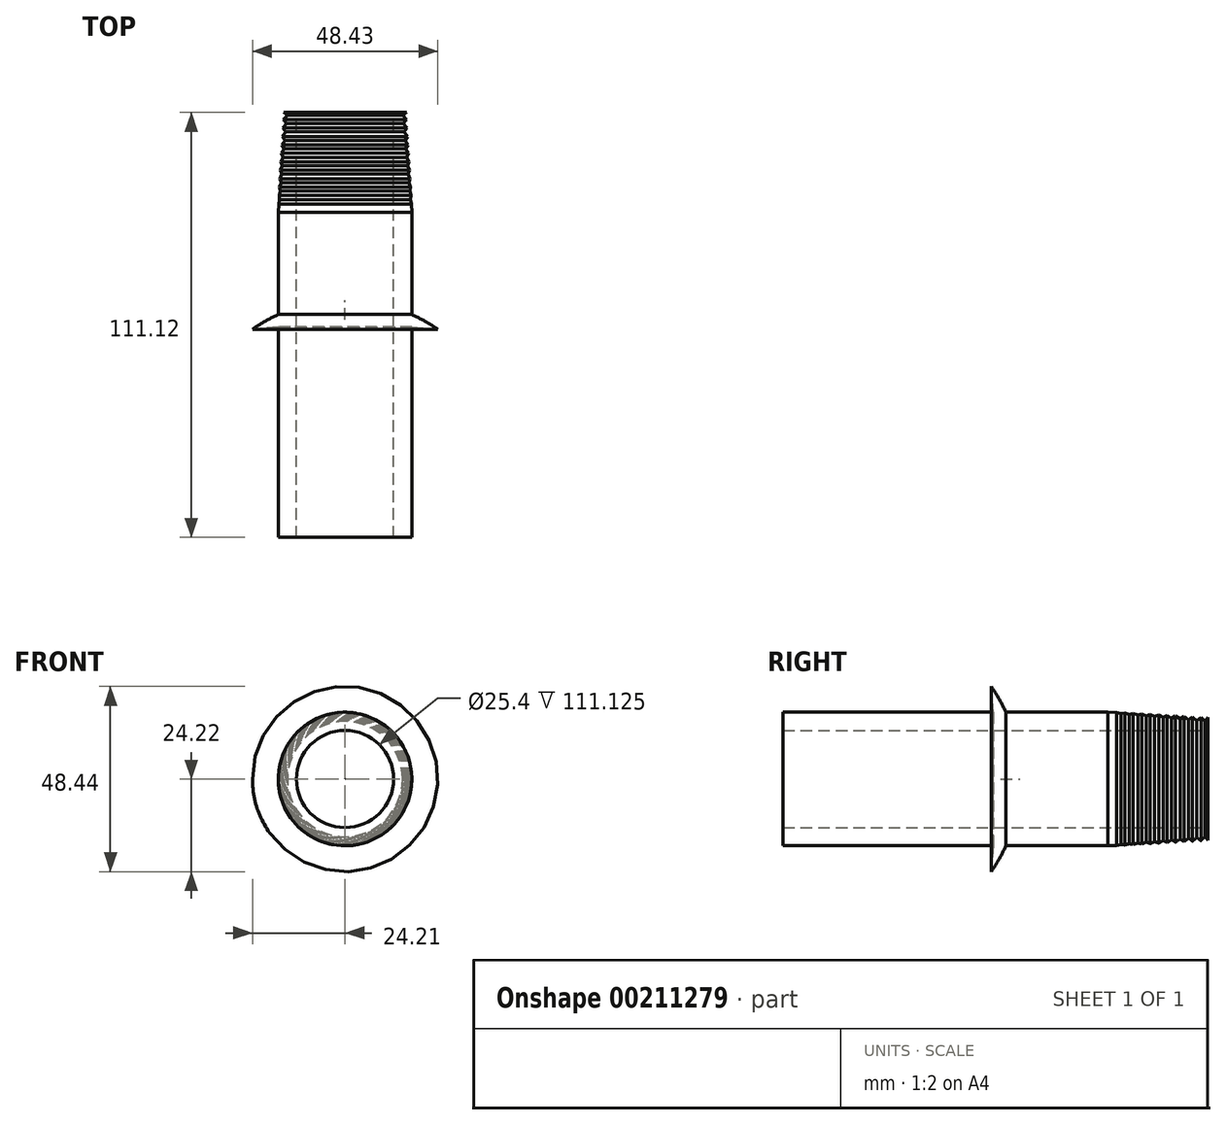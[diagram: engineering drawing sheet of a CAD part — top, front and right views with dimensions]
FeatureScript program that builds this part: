
annotation { "Feature Type Name" : "Feature", "Feature Type Description" : "" }
export const myFeature = defineFeature(function(context is Context, id is Id, definition is map)
    precondition{}
    {
        {
            var Q0;
            Q0=qCreatedBy(makeId("Front.planeOp"),FACE);
            var sketch = newSketch(context, id + "F0", { "sketchPlane" : qUnion([Q0])});
            skCircle(sketch, "E0", {"center": v(0, 0) * mm, "radius": 12.7 * mm});
            skCircle(sketch, "E1", {"center": v(0, 0) * mm, "radius": 17.46 * mm});
            skSolve(sketch);
        }
        {
            var Q0;
            Q0 = qSketchRegion(id + "F0", true);
            extrude(context, id + "F1", {"entities" : qUnion([Q0]), "endBound" : BoundingType.SYMMETRIC, "depth" : 111.12 * mm});
        }
        {
            var Q0;
            Q0=qCreatedBy(makeId("Top.planeOp"),FACE);
            var sketch = newSketch(context, id + "F2", { "sketchPlane" : qUnion([Q0])});
            skLineSegment(sketch, "E2", {"start": v(0, 0) * mm, "end": v(0, -0.61) * mm});
            skArc(sketch, "E3", {"start": v(0, 6.43) * mm, "mid": v(0, 6.43) * mm, "end": v(0, 6.43) * mm});
            skLineSegment(sketch, "E4", {"start": v(-17.44, -0.6) * mm, "end": v(-24.21, -1.16) * mm});
            skLineSegment(sketch, "E5", {"start": v(0, -0.61) * mm, "end": v(0, 6.43) * mm});
            skLineSegment(sketch, "E6", {"start": v(0, 6.43) * mm, "end": v(0, 1.36) * mm});
            skPoint(sketch, "E6.endSnap0", {"position": v(0, 2.9) * mm});
            skLineSegment(sketch, "E7", {"start": v(0, 2.9) * mm, "end": v(0, -0.61) * mm});
            skLineSegment(sketch, "E8", {"start": v(-17.44, -0.6) * mm, "end": v(-17.44, 2.7) * mm});
            skArc(sketch, "E9.trimOffspring", {"start": v(-17.44, 2.7) * mm, "mid": v(-20.92, 0.93) * mm, "end": v(-24.21, -1.16) * mm});
            skPoint(sketch, "E10.orphan", {"position": v(0, -8.52) * mm});
            skPoint(sketch, "E11.orphan", {"position": v(0, 13.95) * mm});
            skSolve(sketch);
        }
        {
            var Q0;
            Q0 = qSketchRegion(id + "F2", true);
            var Q1;
            Q1=sQuery(id+"F2.wireOp",EDGE,"E6");
            revolve(context, id + "F3", {"operationType" : NewBodyOperationType.ADD, "entities" : qUnion([Q0]), "axis" : qUnion([Q1]), "revolveType" : RevolveType.FULL});
        }
        {
            var Q0;
            Q0=qCreatedBy(makeId("Top.planeOp"),FACE);
            var sketch = newSketch(context, id + "F4", { "sketchPlane" : qUnion([Q0])});
            skLineSegment(sketch, "E12", {"start": v(0, 72.15) * mm, "end": v(0, 29.4) * mm});
            skPoint(sketch, "E13.endSnap0", {"position": v(-17.46, 43.77) * mm});
            skPoint(sketch, "E14.endSnap0", {"position": v(-17.46, 50.4) * mm});
            skLineSegment(sketch, "E15", {"start": v(-16.05, 55.55) * mm, "end": v(-15.06, 54.8) * mm});
            skLineSegment(sketch, "E16", {"start": v(-15.06, 54.8) * mm, "end": v(-16.15, 53.7) * mm});
            skLineSegment(sketch, "E17", {"start": v(-16.15, 53.7) * mm, "end": v(-15.26, 52.66) * mm});
            skLineSegment(sketch, "E18", {"start": v(-15.26, 52.66) * mm, "end": v(-16.27, 51.5) * mm});
            skLineSegment(sketch, "E19", {"start": v(-16.27, 51.5) * mm, "end": v(-15.47, 50.45) * mm});
            skLineSegment(sketch, "E20", {"start": v(-15.47, 50.45) * mm, "end": v(-16.38, 49.3) * mm});
            skLineSegment(sketch, "E21", {"start": v(-16.38, 49.3) * mm, "end": v(-15.68, 48.24) * mm});
            skLineSegment(sketch, "E22", {"start": v(-15.68, 48.24) * mm, "end": v(-16.5, 47.08) * mm});
            skLineSegment(sketch, "E23", {"start": v(-16.5, 47.08) * mm, "end": v(-15.89, 46.03) * mm});
            skLineSegment(sketch, "E24", {"start": v(-15.89, 46.03) * mm, "end": v(-16.62, 44.88) * mm});
            skLineSegment(sketch, "E25", {"start": v(-16.62, 44.88) * mm, "end": v(-16.1, 43.82) * mm});
            skLineSegment(sketch, "E26", {"start": v(-16.1, 43.82) * mm, "end": v(-16.74, 42.67) * mm});
            skLineSegment(sketch, "E27", {"start": v(-16.74, 42.67) * mm, "end": v(-16.38, 41.61) * mm});
            skLineSegment(sketch, "E28", {"start": v(-16.38, 41.61) * mm, "end": v(-16.86, 40.46) * mm});
            skLineSegment(sketch, "E29", {"start": v(-16.86, 40.46) * mm, "end": v(-16.52, 39.4) * mm});
            skLineSegment(sketch, "E30", {"start": v(-16.52, 39.4) * mm, "end": v(-16.98, 38.25) * mm});
            skLineSegment(sketch, "E31", {"start": v(-16.98, 38.25) * mm, "end": v(-16.72, 37.2) * mm});
            skLineSegment(sketch, "E32", {"start": v(-16.72, 37.2) * mm, "end": v(-17.1, 36.04) * mm});
            skLineSegment(sketch, "E33", {"start": v(-17.1, 36.04) * mm, "end": v(-16.93, 34.98) * mm});
            skLineSegment(sketch, "E34", {"start": v(-16.93, 34.98) * mm, "end": v(-17.22, 33.83) * mm});
            skLineSegment(sketch, "E35", {"start": v(-17.22, 33.83) * mm, "end": v(-17.14, 32.77) * mm});
            skLineSegment(sketch, "E36", {"start": v(-17.34, 31.62) * mm, "end": v(-17.46, 29.4) * mm});
            skLineSegment(sketch, "E37", {"start": v(-17.34, 31.62) * mm, "end": v(-17.14, 32.77) * mm});
            skLineSegment(sketch, "E38", {"start": v(-17.46, 29.4) * mm, "end": v(-17.46, 55.55) * mm});
            skLineSegment(sketch, "E39", {"start": v(-16.05, 55.55) * mm, "end": v(-16.3, 55.75) * mm});
            skLineSegment(sketch, "E40", {"start": v(-16.3, 55.75) * mm, "end": v(-17.46, 55.75) * mm});
            skLineSegment(sketch, "E41", {"start": v(-17.46, 55.75) * mm, "end": v(-17.46, 55.27) * mm});
            skSolve(sketch);
        }
        {
            var Q0;
            Q0 = qSketchRegion(id + "F4", true);
            var Q1;
            Q1=sQuery(id+"F4.wireOp",EDGE,"E12");
            revolve(context, id + "F5", {"operationType" : NewBodyOperationType.REMOVE, "entities" : qUnion([Q0]), "axis" : qUnion([Q1]), "revolveType" : RevolveType.FULL, "oppositeDirection" : true});
        }
    });
